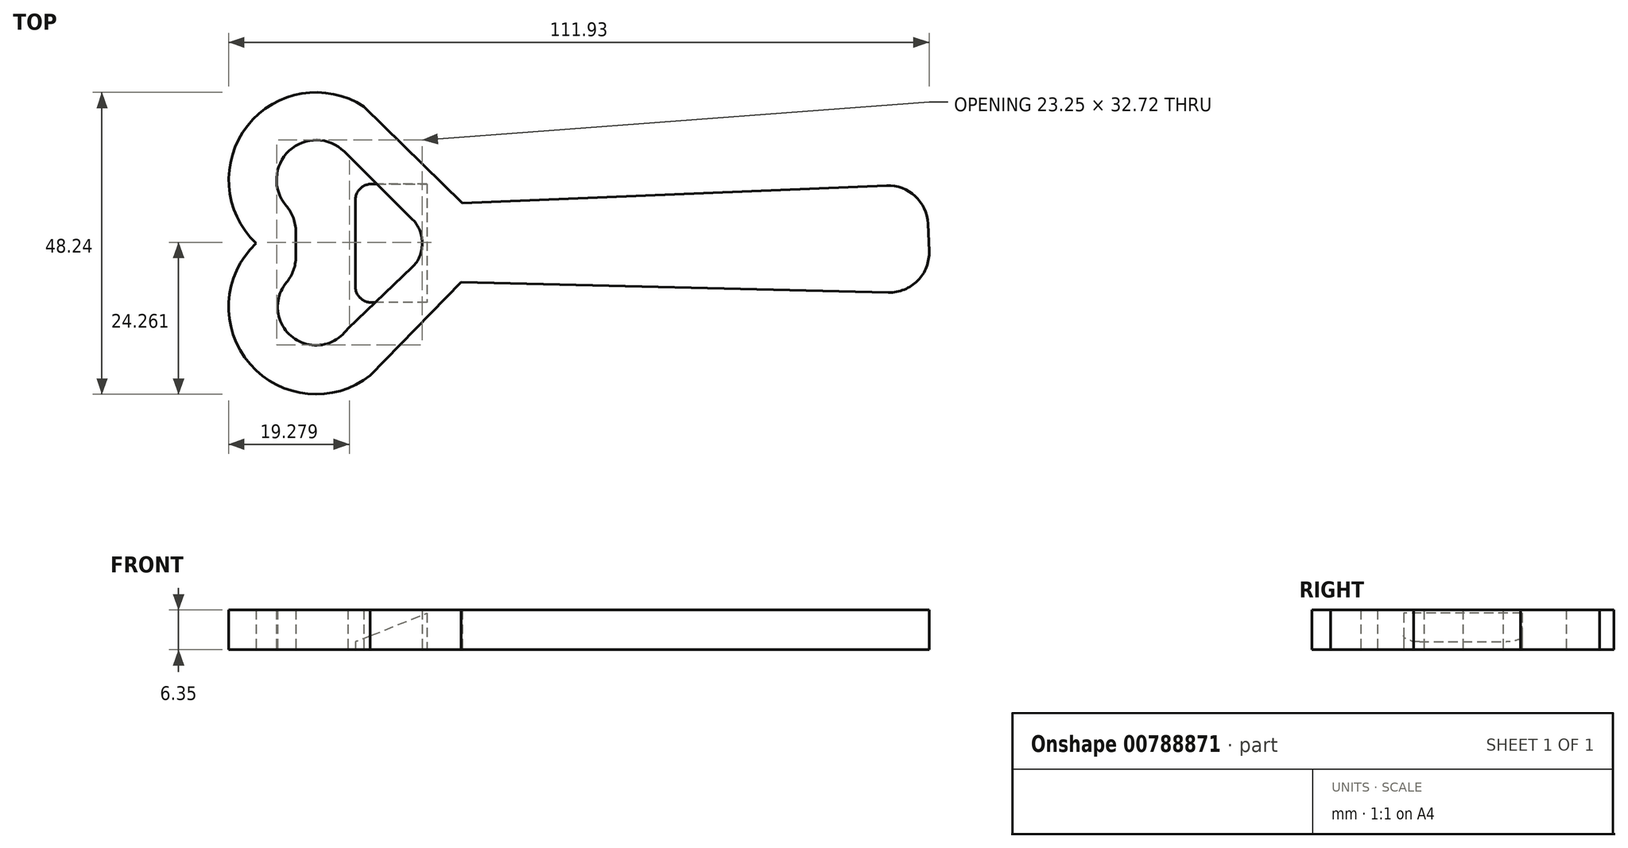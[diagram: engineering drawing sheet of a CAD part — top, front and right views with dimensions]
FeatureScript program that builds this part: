
annotation { "Feature Type Name" : "Feature", "Feature Type Description" : "" }
export const myFeature = defineFeature(function(context is Context, id is Id, definition is map)
    precondition{}
    {
        {
            var Q0;
            Q0=qCreatedBy(makeId("Top.planeOp"),FACE);
            var sketch = newSketch(context, id + "F0", { "sketchPlane" : qUnion([Q0])});
            skLineSegment(sketch, "E0", {"start": v(-19.5, 6.41) * mm, "end": v(48.33, 9.2) * mm});
            skLineSegment(sketch, "E1", {"start": v(54.93, 3.12) * mm, "end": v(55.11, -1.26) * mm});
            skLineSegment(sketch, "E2", {"start": v(48.61, -7.87) * mm, "end": v(-19.66, -6.19) * mm});
            skLineSegment(sketch, "E3", {"start": v(-19.66, -6.19) * mm, "end": v(-34.18, -21.13) * mm});
            skLineSegment(sketch, "E4", {"start": v(-19.5, 6.41) * mm, "end": v(-35.22, 21.86) * mm});
            skArc(sketch, "E5", {"start": v(-31.23, 17.95) * mm, "mid": v(-51.85, 20.8) * mm, "end": v(-52.43, 0) * mm});
            skArc(sketch, "E6", {"start": v(-52.43, 0) * mm, "mid": v(-52.13, -20.6) * mm, "end": v(-31.64, -18.51) * mm});
            skPoint(sketch, "E7.visualSharp", {"position": v(54.67, 9.46) * mm});
            skArc(sketch, "E7.filletArc", {"start": v(54.93, 3.12) * mm, "mid": v(52.9, 7.53) * mm, "end": v(48.33, 9.2) * mm});
            skPoint(sketch, "E8.visualSharp", {"position": v(55.4, -8.03) * mm});
            skArc(sketch, "E8.filletArc", {"start": v(48.61, -7.87) * mm, "mid": v(53.3, -5.97) * mm, "end": v(55.11, -1.26) * mm});
            skArc(sketch, "E9", {"start": v(-38.35, 14.65) * mm, "mid": v(-47.14, 14.79) * mm, "end": v(-47.63, 6) * mm});
            skArc(sketch, "E10", {"start": v(-47.56, -6.23) * mm, "mid": v(-46.56, -15.05) * mm, "end": v(-37.8, -13.66) * mm});
            skLineSegment(sketch, "E11", {"start": v(-46.09, 1.85) * mm, "end": v(-46.09, -2.16) * mm});
            skLineSegment(sketch, "E12", {"start": v(-37.8, -13.66) * mm, "end": v(-27.48, -3.82) * mm});
            skLineSegment(sketch, "E13", {"start": v(-25.9, -0.14) * mm, "end": v(-25.9, 0.17) * mm});
            skLineSegment(sketch, "E14", {"start": v(-27.4, 3.78) * mm, "end": v(-38.35, 14.65) * mm});
            skPoint(sketch, "E15.visualSharp", {"position": v(-46.09, 4.7) * mm});
            skArc(sketch, "E15.filletArc", {"start": v(-46.09, 1.85) * mm, "mid": v(-46.48, 4.07) * mm, "end": v(-47.63, 6) * mm});
            skPoint(sketch, "E16.visualSharp", {"position": v(-46.09, -4.95) * mm});
            skArc(sketch, "E16.filletArc", {"start": v(-47.56, -6.23) * mm, "mid": v(-46.47, -4.33) * mm, "end": v(-46.09, -2.16) * mm});
            skPoint(sketch, "E17.visualSharp", {"position": v(-25.9, 2.29) * mm});
            skArc(sketch, "E17.filletArc", {"start": v(-25.9, 0.17) * mm, "mid": v(-26.3, 2.12) * mm, "end": v(-27.4, 3.78) * mm});
            skPoint(sketch, "E18.visualSharp", {"position": v(-25.9, -2.32) * mm});
            skArc(sketch, "E18.filletArc", {"start": v(-27.48, -3.82) * mm, "mid": v(-26.32, -2.14) * mm, "end": v(-25.9, -0.14) * mm});
            skSolve(sketch);
        }
        {
            var Q0;
            {var subQ8=sQuery(id+"F0.wireOp",EDGE,"E0");Q0=makeQuery(id+"F0.imprint","IMPRINT",FACE,{"disambiguationData":[TD([[makeQuery(id+"F0.imprint","IMPRINT",EDGE,{"derivedFrom":subQ8}),-1.0]])]});}
            extrude(context, id + "F1", {"entities" : qUnion([Q0]), "depth" : 6.35 * mm, "offsetDistance" : 25.4 * mm});
        }
        {
            var Q0;
            Q0=qCreatedBy(makeId("Top.planeOp"),FACE);
            var sketch = newSketch(context, id + "F2", { "sketchPlane" : qUnion([Q0])});
            skLineSegment(sketch, "E19.bottom", {"start": v(-25.13, 9.47) * mm, "end": v(-36.56, 9.47) * mm});
            skLineSegment(sketch, "E19.top", {"start": v(-25.13, -9.47) * mm, "end": v(-36.56, -9.47) * mm});
            skLineSegment(sketch, "E19.left", {"start": v(-25.13, 9.47) * mm, "end": v(-25.13, -9.47) * mm});
            skLineSegment(sketch, "E19.right", {"start": v(-36.56, 9.47) * mm, "end": v(-36.56, -9.47) * mm});
            skPoint(sketch, "E19.middle", {"position": v(-30.85, 0) * mm});
            skPoint(sketch, "E20.visualSharp", {"position": v(-36.56, -9.47) * mm});
            skLineSegment(sketch, "E20.filletArc", {"start": v(-36.56, -9.47) * mm, "end": v(-36.56, -9.47) * mm});
            skPoint(sketch, "E21.visualSharp", {"position": v(-36.56, 9.47) * mm});
            skLineSegment(sketch, "E21.filletArc", {"start": v(-36.56, 9.47) * mm, "end": v(-36.56, 9.47) * mm});
            skSolve(sketch);
        }
        {
            var Q0;
            Q0=makeQuery(id+"F2.imprint","IMPRINT",FACE,{"disambiguationData":[TD([[makeQuery(id+"F2.imprint","IMPRINT",EDGE,{"derivedFrom":sQuery(id+"F2.wireOp",EDGE,"E19.bottom")}),1.0]])]});
            extrude(context, id + "F3", {"entities" : qUnion([Q0]), "depth" : 6.35 * mm, "offsetDistance" : 25.4 * mm});
        }
        {
            var Q0;
            Q0=makeQuery(id+"F3.opExtrude","CAP_EDGE",EDGE,{"disambiguationData":[OSD([sQuery(id+"F2.wireOp",EDGE,"E19.right")])],"isStart":false});
            chamfer(context, id + "F4", {"entities" : qUnion([Q0]), "chamferType" : ChamferType.TWO_OFFSETS, "width1" : 12.7 * mm, "oppositeDirection" : false, "width2" : 5.08 * mm, "tangentPropagation" : true});
        }
        {
            var Q0;
            Q0=makeQuery(id+"F3.opExtrude","SWEPT_EDGE",EDGE,{"disambiguationData":[OSD([sQuery(id+"F2.wireOp",EDGE,"E19.top"),sQuery(id+"F2.wireOp",EDGE,"E19.right")])]});
            var Q1;
            Q1=makeQuery(id+"F3.opExtrude","SWEPT_EDGE",EDGE,{"disambiguationData":[OSD([sQuery(id+"F2.wireOp",EDGE,"E19.bottom"),sQuery(id+"F2.wireOp",EDGE,"E19.right")])]});
            fillet(context, id + "F5", {"entities" : qUnion([Q0, Q1]), "radius" : 2.54 * mm, "tangentPropagation" : true, "allowEdgeOverflow" : false});
        }
    });
